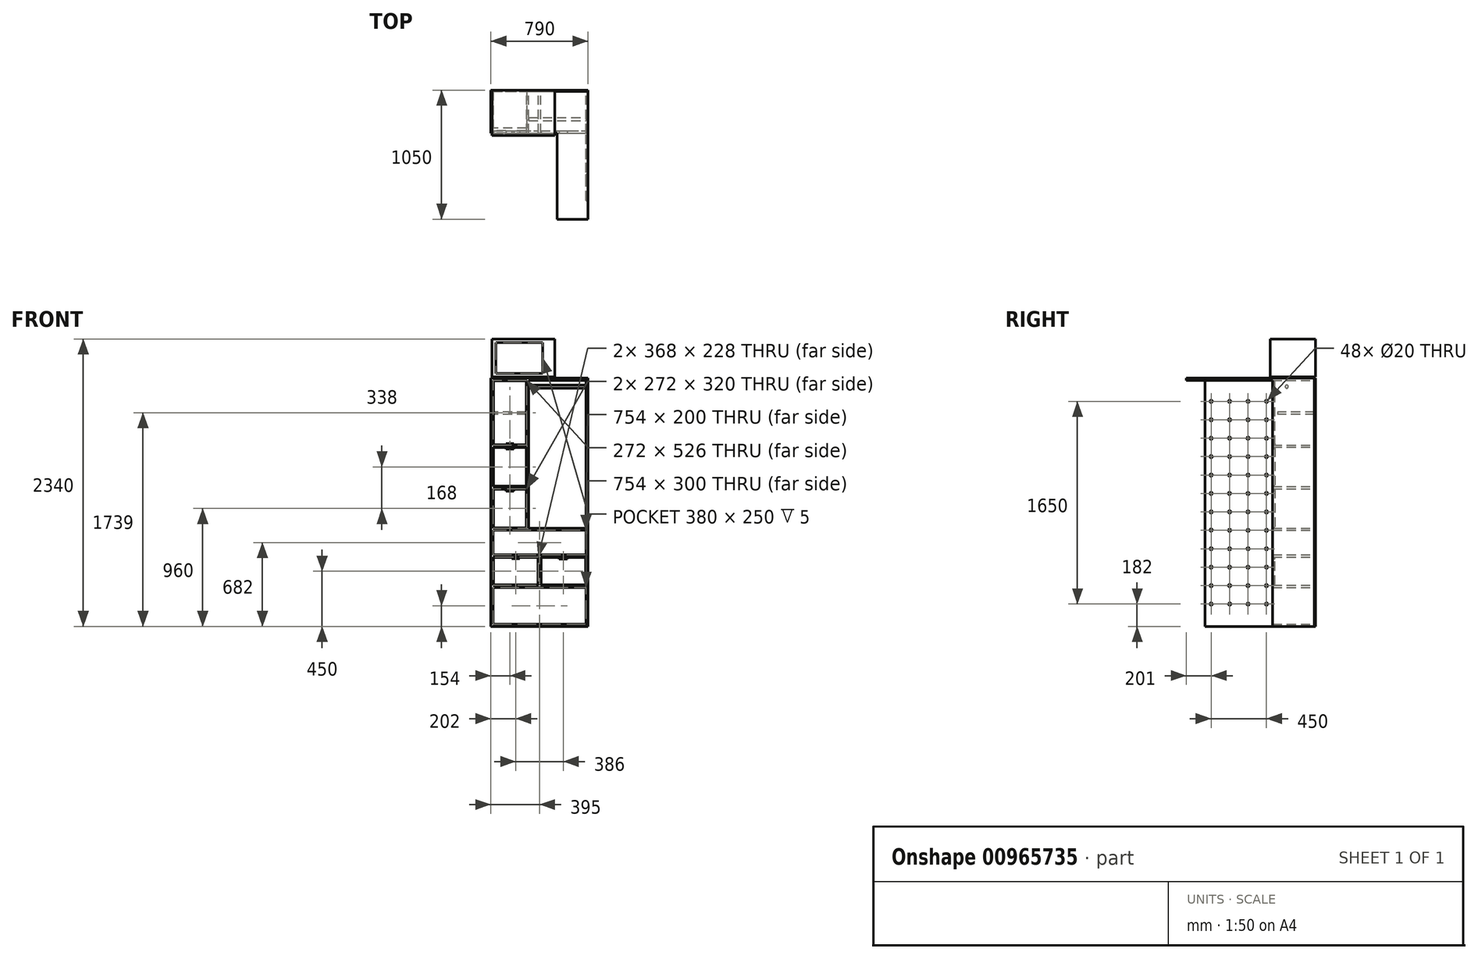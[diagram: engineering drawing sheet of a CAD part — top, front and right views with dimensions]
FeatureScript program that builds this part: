
annotation { "Feature Type Name" : "Feature", "Feature Type Description" : "" }
export const myFeature = defineFeature(function(context is Context, id is Id, definition is map)
    precondition{}
    {
        {
            var Q0;
            Q0=qCreatedBy(makeId("Front.planeOp"),FACE);
            var sketch = newSketch(context, id + "F0", { "sketchPlane" : qUnion([Q0])});
            skLineSegment(sketch, "E0.bottom", {"start": v(0, 0) * mm, "end": v(790, 0) * mm});
            skLineSegment(sketch, "E0.top", {"start": v(0, 2020) * mm, "end": v(790, 2020) * mm});
            skLineSegment(sketch, "E0.left", {"start": v(0, 0) * mm, "end": v(0, 2020) * mm});
            skLineSegment(sketch, "E0.right", {"start": v(790, 0) * mm, "end": v(790, 2020) * mm});
            skLineSegment(sketch, "E1.0", {"start": v(18, 2002) * mm, "end": v(290, 2002) * mm});
            skLineSegment(sketch, "E1.1", {"start": v(18, 18) * mm, "end": v(18, 318) * mm});
            skLineSegment(sketch, "E1.2", {"start": v(18, 18) * mm, "end": v(772, 18) * mm});
            skLineSegment(sketch, "E1.3", {"start": v(772, 18) * mm, "end": v(772, 318) * mm});
            skLineSegment(sketch, "E2.bottom", {"start": v(18, 318) * mm, "end": v(772, 318) * mm});
            skLineSegment(sketch, "E2.top", {"start": v(18, 336) * mm, "end": v(386, 336) * mm});
            skLineSegment(sketch, "E3.bottom", {"start": v(18, 564) * mm, "end": v(386, 564) * mm});
            skLineSegment(sketch, "E3.top", {"start": v(18, 582) * mm, "end": v(772, 582) * mm});
            skLineSegment(sketch, "E4.bottom", {"start": v(18, 782) * mm, "end": v(772, 782) * mm});
            skLineSegment(sketch, "E4.top", {"start": v(18, 800) * mm, "end": v(290, 800) * mm});
            skLineSegment(sketch, "E5.left", {"start": v(308, 2002) * mm, "end": v(308, 800) * mm});
            skLineSegment(sketch, "E5.right", {"start": v(290, 2002) * mm, "end": v(290, 1476) * mm});
            skLineSegment(sketch, "E6.bottom", {"start": v(18, 1120) * mm, "end": v(290, 1120) * mm});
            skLineSegment(sketch, "E6.top", {"start": v(18, 1138) * mm, "end": v(290, 1138) * mm});
            skLineSegment(sketch, "E7.bottom", {"start": v(290, 1458) * mm, "end": v(18, 1458) * mm});
            skLineSegment(sketch, "E7.top", {"start": v(290, 1476) * mm, "end": v(18, 1476) * mm});
            skLineSegment(sketch, "E8.trimOffspring", {"start": v(308, 2002) * mm, "end": v(772, 2002) * mm});
            skLineSegment(sketch, "E9.trimOffspring", {"start": v(290, 1458) * mm, "end": v(290, 1138) * mm});
            skLineSegment(sketch, "E10.trimOffspring", {"start": v(18, 1476) * mm, "end": v(18, 2002) * mm});
            skLineSegment(sketch, "E11.trimOffspring", {"start": v(18, 1138) * mm, "end": v(18, 1458) * mm});
            skLineSegment(sketch, "E12.trimOffspring", {"start": v(290, 1120) * mm, "end": v(290, 800) * mm});
            skLineSegment(sketch, "E13.trimOffspring", {"start": v(18, 800) * mm, "end": v(18, 1120) * mm});
            skLineSegment(sketch, "E14.trimOffspring", {"start": v(308, 800) * mm, "end": v(772, 800) * mm});
            skLineSegment(sketch, "E15.trimOffspring", {"start": v(772, 800) * mm, "end": v(772, 2002) * mm});
            skLineSegment(sketch, "E16.trimOffspring", {"start": v(772, 582) * mm, "end": v(772, 782) * mm});
            skLineSegment(sketch, "E17.trimOffspring", {"start": v(18, 582) * mm, "end": v(18, 782) * mm});
            skLineSegment(sketch, "E18.trimOffspring", {"start": v(18, 336) * mm, "end": v(18, 564) * mm});
            skLineSegment(sketch, "E19.trimOffspring", {"start": v(772, 336) * mm, "end": v(772, 564) * mm});
            skLineSegment(sketch, "E20.left", {"start": v(386, 564) * mm, "end": v(386, 336) * mm});
            skLineSegment(sketch, "E20.right", {"start": v(404, 564) * mm, "end": v(404, 336) * mm});
            skLineSegment(sketch, "E21.trimOffspring", {"start": v(404, 564) * mm, "end": v(772, 564) * mm});
            skLineSegment(sketch, "E22.trimOffspring", {"start": v(404, 336) * mm, "end": v(772, 336) * mm});
            skSolve(sketch);
        }
        {
            var Q0;
            Q0 = qSketchRegion(id + "F0", true);
            extrude(context, id + "F1", {"entities" : qUnion([Q0]), "depth" : 340 * mm, "offsetDistance" : 25 * mm});
        }
        {
            var Q0;
            Q0=makeQuery(id+"F1.opExtrude","CAP_FACE",FACE,{"disambiguationData":[OSD([sQuery(id+"F0.wireOp",EDGE,"E0.bottom"),sQuery(id+"F0.wireOp",EDGE,"E0.top"),sQuery(id+"F0.wireOp",EDGE,"E0.left"),sQuery(id+"F0.wireOp",EDGE,"E0.right"),sQuery(id+"F0.wireOp",EDGE,"E1.0"),sQuery(id+"F0.wireOp",EDGE,"E1.1"),sQuery(id+"F0.wireOp",EDGE,"E1.2"),sQuery(id+"F0.wireOp",EDGE,"E1.3"),sQuery(id+"F0.wireOp",EDGE,"E2.bottom"),sQuery(id+"F0.wireOp",EDGE,"E2.top"),sQuery(id+"F0.wireOp",EDGE,"E3.bottom"),sQuery(id+"F0.wireOp",EDGE,"E3.top"),sQuery(id+"F0.wireOp",EDGE,"E4.bottom"),sQuery(id+"F0.wireOp",EDGE,"E4.top"),sQuery(id+"F0.wireOp",EDGE,"E5.left"),sQuery(id+"F0.wireOp",EDGE,"E5.right"),sQuery(id+"F0.wireOp",EDGE,"E6.bottom"),sQuery(id+"F0.wireOp",EDGE,"E6.top"),sQuery(id+"F0.wireOp",EDGE,"E7.bottom"),sQuery(id+"F0.wireOp",EDGE,"E7.top"),sQuery(id+"F0.wireOp",EDGE,"E8.trimOffspring"),sQuery(id+"F0.wireOp",EDGE,"E9.trimOffspring"),sQuery(id+"F0.wireOp",EDGE,"E10.trimOffspring"),sQuery(id+"F0.wireOp",EDGE,"E11.trimOffspring"),sQuery(id+"F0.wireOp",EDGE,"E12.trimOffspring"),sQuery(id+"F0.wireOp",EDGE,"E13.trimOffspring"),sQuery(id+"F0.wireOp",EDGE,"E14.trimOffspring"),sQuery(id+"F0.wireOp",EDGE,"E15.trimOffspring"),sQuery(id+"F0.wireOp",EDGE,"E16.trimOffspring"),sQuery(id+"F0.wireOp",EDGE,"E17.trimOffspring"),sQuery(id+"F0.wireOp",EDGE,"E18.trimOffspring"),sQuery(id+"F0.wireOp",EDGE,"E19.trimOffspring"),sQuery(id+"F0.wireOp",EDGE,"E20.left"),sQuery(id+"F0.wireOp",EDGE,"E20.right"),sQuery(id+"F0.wireOp",EDGE,"E21.trimOffspring"),sQuery(id+"F0.wireOp",EDGE,"E22.trimOffspring")])],"isStart":true});
            var sketch = newSketch(context, id + "F2", { "sketchPlane" : qUnion([Q0])});
            skLineSegment(sketch, "E23.bottom", {"start": v(-790, 2020) * mm, "end": v(0, 2020) * mm});
            skLineSegment(sketch, "E23.top", {"start": v(-790, 0) * mm, "end": v(0, 0) * mm});
            skLineSegment(sketch, "E23.left", {"start": v(-790, 2020) * mm, "end": v(-790, 0) * mm});
            skLineSegment(sketch, "E23.right", {"start": v(0, 2020) * mm, "end": v(0, 0) * mm});
            skSolve(sketch);
        }
        {
            var Q0;
            Q0 = qSketchRegion(id + "F2", true);
            extrude(context, id + "F3", {"entities" : qUnion([Q0]), "depth" : 9 * mm, "offsetDistance" : 25 * mm});
        }
        {
            var Q0;
            Q0=makeQuery(id+"F1.opExtrude","SWEPT_FACE",FACE,{"disambiguationData":[OSD([sQuery(id+"F0.wireOp",EDGE,"E0.top")])]});
            var sketch = newSketch(context, id + "F4", { "sketchPlane" : qUnion([Q0])});
            skLineSegment(sketch, "E24.bottom", {"start": v(790, -340) * mm, "end": v(540, -340) * mm});
            skLineSegment(sketch, "E24.top", {"start": v(790, -1041) * mm, "end": v(540, -1041) * mm});
            skLineSegment(sketch, "E24.left", {"start": v(790, -340) * mm, "end": v(790, -1041) * mm});
            skLineSegment(sketch, "E24.right", {"start": v(540, -340) * mm, "end": v(540, -1041) * mm});
            skSolve(sketch);
        }
        {
            var Q0;
            Q0 = qSketchRegion(id + "F4", true);
            extrude(context, id + "F5", {"entities" : qUnion([Q0]), "operationType" : NewBodyOperationType.ADD, "oppositeDirection" : true, "depth" : 18 * mm, "offsetDistance" : 25 * mm});
        }
        {
            var Q0;
            Q0=makeQuery(id+"F5.boolean.opBoolean","MERGE",FACE,{"derivedFrom":[makeQuery(id+"F1.opExtrude","SWEPT_FACE",FACE,{"disambiguationData":[OSD([sQuery(id+"F0.wireOp",EDGE,"E8.trimOffspring")])]}),makeQuery(id+"F5.opExtrude","CAP_FACE",FACE,{"disambiguationData":[OSD([sQuery(id+"F4.wireOp",EDGE,"E24.bottom"),sQuery(id+"F4.wireOp",EDGE,"E24.top"),sQuery(id+"F4.wireOp",EDGE,"E24.left"),sQuery(id+"F4.wireOp",EDGE,"E24.right")])],"isStart":false})]});
            var sketch = newSketch(context, id + "F6", { "sketchPlane" : qUnion([Q0])});
            skLineSegment(sketch, "E25.bottom", {"start": v(772, 340) * mm, "end": v(790, 340) * mm});
            skLineSegment(sketch, "E25.top", {"start": v(772, 890) * mm, "end": v(790, 890) * mm});
            skLineSegment(sketch, "E25.left", {"start": v(772, 340) * mm, "end": v(772, 890) * mm});
            skLineSegment(sketch, "E25.right", {"start": v(790, 340) * mm, "end": v(790, 890) * mm});
            skSolve(sketch);
        }
        {
            var Q0;
            Q0 = qSketchRegion(id + "F6", true);
            extrude(context, id + "F7", {"entities" : qUnion([Q0]), "depth" : 2002 * mm, "offsetDistance" : 25 * mm});
        }
        {
            var Q0;
            Q0=makeQuery(id+"F7.opExtrude","SWEPT_FACE",FACE,{"disambiguationData":[OSD([sQuery(id+"F6.wireOp",EDGE,"E25.left")])]});
            var sketch = newSketch(context, id + "F8", { "sketchPlane" : qUnion([Q0])});
            skLineSegment(sketch, "E26.bottom", {"start": v(890, 0) * mm, "end": v(340, 0) * mm, "construction": true});
            skLineSegment(sketch, "E26.top", {"start": v(890, 2002) * mm, "end": v(340, 2002) * mm, "construction": true});
            skLineSegment(sketch, "E26.left", {"start": v(890, 0) * mm, "end": v(890, 2002) * mm, "construction": true});
            skLineSegment(sketch, "E26.right", {"start": v(340, 0) * mm, "end": v(340, 2002) * mm, "construction": true});
            skLineSegment(sketch, "E27", {"start": v(390, 2002) * mm, "end": v(390, 0) * mm, "construction": true});
            skLineSegment(sketch, "E28", {"start": v(540, 2002) * mm, "end": v(540, 0) * mm, "construction": true});
            skLineSegment(sketch, "E29", {"start": v(690, 2002) * mm, "end": v(690, 0) * mm, "construction": true});
            skLineSegment(sketch, "E30", {"start": v(840, 2002) * mm, "end": v(840, 0) * mm, "construction": true});
            skLineSegment(sketch, "E31", {"start": v(340, 1832) * mm, "end": v(890, 1832) * mm, "construction": true});
            skLineSegment(sketch, "E32", {"start": v(340, 1682) * mm, "end": v(890, 1682) * mm, "construction": true});
            skLineSegment(sketch, "E33", {"start": v(340, 1532) * mm, "end": v(890, 1532) * mm, "construction": true});
            skLineSegment(sketch, "E34", {"start": v(340, 1382) * mm, "end": v(890, 1382) * mm, "construction": true});
            skLineSegment(sketch, "E35", {"start": v(340, 1232) * mm, "end": v(890, 1232) * mm, "construction": true});
            skLineSegment(sketch, "E36", {"start": v(340, 1082) * mm, "end": v(890, 1082) * mm, "construction": true});
            skLineSegment(sketch, "E37", {"start": v(340, 932) * mm, "end": v(890, 932) * mm, "construction": true});
            skLineSegment(sketch, "E38", {"start": v(340, 782) * mm, "end": v(890, 782) * mm, "construction": true});
            skLineSegment(sketch, "E39", {"start": v(340, 632) * mm, "end": v(890, 632) * mm, "construction": true});
            skLineSegment(sketch, "E40", {"start": v(340, 482) * mm, "end": v(890, 482) * mm, "construction": true});
            skLineSegment(sketch, "E41", {"start": v(340, 332) * mm, "end": v(890, 332) * mm, "construction": true});
            skLineSegment(sketch, "E42", {"start": v(340, 182) * mm, "end": v(890, 182) * mm, "construction": true});
            skCircle(sketch, "E43", {"center": v(390, 1832) * mm, "radius": 10 * mm});
            skCircle(sketch, "E44", {"center": v(540, 1832) * mm, "radius": 10 * mm});
            skCircle(sketch, "E45", {"center": v(690, 1832) * mm, "radius": 10 * mm});
            skCircle(sketch, "E46", {"center": v(840, 1832) * mm, "radius": 10 * mm});
            skCircle(sketch, "E47", {"center": v(840, 1682) * mm, "radius": 10 * mm});
            skCircle(sketch, "E48", {"center": v(840, 1532) * mm, "radius": 10 * mm});
            skCircle(sketch, "E49", {"center": v(840, 1382) * mm, "radius": 10 * mm});
            skCircle(sketch, "E50", {"center": v(840, 1232) * mm, "radius": 10 * mm});
            skCircle(sketch, "E51", {"center": v(840, 1082) * mm, "radius": 10 * mm});
            skCircle(sketch, "E52", {"center": v(840, 932) * mm, "radius": 10 * mm});
            skCircle(sketch, "E53", {"center": v(840, 784.34) * mm, "radius": 10 * mm});
            skCircle(sketch, "E54", {"center": v(840, 632) * mm, "radius": 10 * mm});
            skCircle(sketch, "E55", {"center": v(840, 482) * mm, "radius": 10 * mm});
            skCircle(sketch, "E56", {"center": v(840, 332) * mm, "radius": 10 * mm});
            skCircle(sketch, "E57", {"center": v(840, 182) * mm, "radius": 10 * mm});
            skCircle(sketch, "E58", {"center": v(688.75, 182) * mm, "radius": 10 * mm});
            skCircle(sketch, "E59", {"center": v(540, 182) * mm, "radius": 10 * mm});
            skCircle(sketch, "E60", {"center": v(390, 182) * mm, "radius": 10 * mm});
            skCircle(sketch, "E61", {"center": v(390, 332) * mm, "radius": 10 * mm});
            skCircle(sketch, "E62", {"center": v(540, 332) * mm, "radius": 10 * mm});
            skCircle(sketch, "E63", {"center": v(690, 332) * mm, "radius": 10 * mm});
            skCircle(sketch, "E64", {"center": v(690, 482) * mm, "radius": 10 * mm});
            skCircle(sketch, "E65", {"center": v(540, 482) * mm, "radius": 10 * mm});
            skCircle(sketch, "E66", {"center": v(390, 482) * mm, "radius": 10 * mm});
            skCircle(sketch, "E67", {"center": v(390, 632) * mm, "radius": 10 * mm});
            skCircle(sketch, "E68", {"center": v(540, 632) * mm, "radius": 10 * mm});
            skCircle(sketch, "E69", {"center": v(690, 632) * mm, "radius": 10 * mm});
            skCircle(sketch, "E70", {"center": v(690, 782) * mm, "radius": 10 * mm});
            skCircle(sketch, "E71", {"center": v(540, 782) * mm, "radius": 10 * mm});
            skCircle(sketch, "E72", {"center": v(390, 782) * mm, "radius": 10 * mm});
            skCircle(sketch, "E73", {"center": v(390, 932) * mm, "radius": 10 * mm});
            skCircle(sketch, "E74", {"center": v(540, 932) * mm, "radius": 10 * mm});
            skCircle(sketch, "E75", {"center": v(690, 932) * mm, "radius": 10 * mm});
            skCircle(sketch, "E76", {"center": v(691.04, 1082) * mm, "radius": 10 * mm});
            skCircle(sketch, "E77", {"center": v(540, 1082) * mm, "radius": 10 * mm});
            skCircle(sketch, "E78", {"center": v(390, 1082) * mm, "radius": 10 * mm});
            skCircle(sketch, "E79", {"center": v(390, 1232) * mm, "radius": 10 * mm});
            skCircle(sketch, "E80", {"center": v(390, 1382) * mm, "radius": 10 * mm});
            skCircle(sketch, "E81", {"center": v(390, 1532) * mm, "radius": 10 * mm});
            skCircle(sketch, "E82", {"center": v(390, 1682) * mm, "radius": 10 * mm});
            skCircle(sketch, "E83", {"center": v(540, 1682) * mm, "radius": 10 * mm});
            skCircle(sketch, "E84", {"center": v(540, 1532) * mm, "radius": 10 * mm});
            skCircle(sketch, "E85", {"center": v(540, 1382) * mm, "radius": 10 * mm});
            skCircle(sketch, "E86", {"center": v(540, 1232) * mm, "radius": 10 * mm});
            skCircle(sketch, "E87", {"center": v(690, 1232) * mm, "radius": 10 * mm});
            skCircle(sketch, "E88", {"center": v(690, 1382) * mm, "radius": 10 * mm});
            skCircle(sketch, "E89", {"center": v(690, 1532) * mm, "radius": 10 * mm});
            skCircle(sketch, "E90", {"center": v(690, 1682) * mm, "radius": 10 * mm});
            skSolve(sketch);
        }
        {
            var Q0;
            Q0 = qSketchRegion(id + "F8", true);
            extrude(context, id + "F9", {"entities" : qUnion([Q0]), "operationType" : NewBodyOperationType.REMOVE, "oppositeDirection" : true, "depth" : 18 * mm, "offsetDistance" : 25 * mm});
        }
        {
            var Q0;
            Q0=makeQuery(id+"F9.boolean.opBoolean","COPY",EDGE,{"derivedFrom":makeQuery(id+"F9.opExtrude","CAP_EDGE",EDGE,{"disambiguationData":[OSD([sQuery(id+"F8.wireOp",EDGE,"E43")])],"isStart":true})});
            var Q1;
            Q1=makeQuery(id+"F9.boolean.opBoolean","COPY",EDGE,{"derivedFrom":makeQuery(id+"F9.opExtrude","CAP_EDGE",EDGE,{"disambiguationData":[OSD([sQuery(id+"F8.wireOp",EDGE,"E44")])],"isStart":true})});
            var Q2;
            Q2=makeQuery(id+"F9.boolean.opBoolean","COPY",EDGE,{"derivedFrom":makeQuery(id+"F9.opExtrude","CAP_EDGE",EDGE,{"disambiguationData":[OSD([sQuery(id+"F8.wireOp",EDGE,"E45")])],"isStart":true})});
            var Q3;
            Q3=makeQuery(id+"F9.boolean.opBoolean","COPY",EDGE,{"derivedFrom":makeQuery(id+"F9.opExtrude","CAP_EDGE",EDGE,{"disambiguationData":[OSD([sQuery(id+"F8.wireOp",EDGE,"E46")])],"isStart":true})});
            var Q4;
            Q4=makeQuery(id+"F9.boolean.opBoolean","COPY",EDGE,{"derivedFrom":makeQuery(id+"F9.opExtrude","CAP_EDGE",EDGE,{"disambiguationData":[OSD([sQuery(id+"F8.wireOp",EDGE,"E47")])],"isStart":true})});
            var Q5;
            Q5=makeQuery(id+"F9.boolean.opBoolean","COPY",EDGE,{"derivedFrom":makeQuery(id+"F9.opExtrude","CAP_EDGE",EDGE,{"disambiguationData":[OSD([sQuery(id+"F8.wireOp",EDGE,"E90")])],"isStart":true})});
            var Q6;
            Q6=makeQuery(id+"F9.boolean.opBoolean","COPY",EDGE,{"derivedFrom":makeQuery(id+"F9.opExtrude","CAP_EDGE",EDGE,{"disambiguationData":[OSD([sQuery(id+"F8.wireOp",EDGE,"E83")])],"isStart":true})});
            var Q7;
            Q7=makeQuery(id+"F9.boolean.opBoolean","COPY",EDGE,{"derivedFrom":makeQuery(id+"F9.opExtrude","CAP_EDGE",EDGE,{"disambiguationData":[OSD([sQuery(id+"F8.wireOp",EDGE,"E82")])],"isStart":true})});
            var Q8;
            Q8=makeQuery(id+"F9.boolean.opBoolean","COPY",EDGE,{"derivedFrom":makeQuery(id+"F9.opExtrude","CAP_EDGE",EDGE,{"disambiguationData":[OSD([sQuery(id+"F8.wireOp",EDGE,"E81")])],"isStart":true})});
            var Q9;
            Q9=makeQuery(id+"F9.boolean.opBoolean","COPY",EDGE,{"derivedFrom":makeQuery(id+"F9.opExtrude","CAP_EDGE",EDGE,{"disambiguationData":[OSD([sQuery(id+"F8.wireOp",EDGE,"E84")])],"isStart":true})});
            var Q10;
            Q10=makeQuery(id+"F9.boolean.opBoolean","COPY",EDGE,{"derivedFrom":makeQuery(id+"F9.opExtrude","CAP_EDGE",EDGE,{"disambiguationData":[OSD([sQuery(id+"F8.wireOp",EDGE,"E89")])],"isStart":true})});
            var Q11;
            Q11=makeQuery(id+"F9.boolean.opBoolean","COPY",EDGE,{"derivedFrom":makeQuery(id+"F9.opExtrude","CAP_EDGE",EDGE,{"disambiguationData":[OSD([sQuery(id+"F8.wireOp",EDGE,"E48")])],"isStart":true})});
            var Q12;
            Q12=makeQuery(id+"F9.boolean.opBoolean","COPY",EDGE,{"derivedFrom":makeQuery(id+"F9.opExtrude","CAP_EDGE",EDGE,{"disambiguationData":[OSD([sQuery(id+"F8.wireOp",EDGE,"E49")])],"isStart":true})});
            var Q13;
            Q13=makeQuery(id+"F9.boolean.opBoolean","COPY",EDGE,{"derivedFrom":makeQuery(id+"F9.opExtrude","CAP_EDGE",EDGE,{"disambiguationData":[OSD([sQuery(id+"F8.wireOp",EDGE,"E88")])],"isStart":true})});
            var Q14;
            Q14=makeQuery(id+"F9.boolean.opBoolean","COPY",EDGE,{"derivedFrom":makeQuery(id+"F9.opExtrude","CAP_EDGE",EDGE,{"disambiguationData":[OSD([sQuery(id+"F8.wireOp",EDGE,"E85")])],"isStart":true})});
            var Q15;
            Q15=makeQuery(id+"F9.boolean.opBoolean","COPY",EDGE,{"derivedFrom":makeQuery(id+"F9.opExtrude","CAP_EDGE",EDGE,{"disambiguationData":[OSD([sQuery(id+"F8.wireOp",EDGE,"E80")])],"isStart":true})});
            var Q16;
            Q16=makeQuery(id+"F9.boolean.opBoolean","COPY",EDGE,{"derivedFrom":makeQuery(id+"F9.opExtrude","CAP_EDGE",EDGE,{"disambiguationData":[OSD([sQuery(id+"F8.wireOp",EDGE,"E79")])],"isStart":true})});
            var Q17;
            Q17=makeQuery(id+"F9.boolean.opBoolean","COPY",EDGE,{"derivedFrom":makeQuery(id+"F9.opExtrude","CAP_EDGE",EDGE,{"disambiguationData":[OSD([sQuery(id+"F8.wireOp",EDGE,"E86")])],"isStart":true})});
            var Q18;
            Q18=makeQuery(id+"F9.boolean.opBoolean","COPY",EDGE,{"derivedFrom":makeQuery(id+"F9.opExtrude","CAP_EDGE",EDGE,{"disambiguationData":[OSD([sQuery(id+"F8.wireOp",EDGE,"E87")])],"isStart":true})});
            var Q19;
            Q19=makeQuery(id+"F9.boolean.opBoolean","COPY",EDGE,{"derivedFrom":makeQuery(id+"F9.opExtrude","CAP_EDGE",EDGE,{"disambiguationData":[OSD([sQuery(id+"F8.wireOp",EDGE,"E50")])],"isStart":true})});
            var Q20;
            Q20=makeQuery(id+"F9.boolean.opBoolean","COPY",EDGE,{"derivedFrom":makeQuery(id+"F9.opExtrude","CAP_EDGE",EDGE,{"disambiguationData":[OSD([sQuery(id+"F8.wireOp",EDGE,"E51")])],"isStart":true})});
            var Q21;
            Q21=makeQuery(id+"F9.boolean.opBoolean","COPY",EDGE,{"derivedFrom":makeQuery(id+"F9.opExtrude","CAP_EDGE",EDGE,{"disambiguationData":[OSD([sQuery(id+"F8.wireOp",EDGE,"E76")])],"isStart":true})});
            var Q22;
            Q22=makeQuery(id+"F9.boolean.opBoolean","COPY",EDGE,{"derivedFrom":makeQuery(id+"F9.opExtrude","CAP_EDGE",EDGE,{"disambiguationData":[OSD([sQuery(id+"F8.wireOp",EDGE,"E77")])],"isStart":true})});
            var Q23;
            Q23=makeQuery(id+"F9.boolean.opBoolean","COPY",EDGE,{"derivedFrom":makeQuery(id+"F9.opExtrude","CAP_EDGE",EDGE,{"disambiguationData":[OSD([sQuery(id+"F8.wireOp",EDGE,"E78")])],"isStart":true})});
            var Q24;
            Q24=makeQuery(id+"F9.boolean.opBoolean","COPY",EDGE,{"derivedFrom":makeQuery(id+"F9.opExtrude","CAP_EDGE",EDGE,{"disambiguationData":[OSD([sQuery(id+"F8.wireOp",EDGE,"E73")])],"isStart":true})});
            var Q25;
            Q25=makeQuery(id+"F9.boolean.opBoolean","COPY",EDGE,{"derivedFrom":makeQuery(id+"F9.opExtrude","CAP_EDGE",EDGE,{"disambiguationData":[OSD([sQuery(id+"F8.wireOp",EDGE,"E74")])],"isStart":false})});
            var Q26;
            Q26=makeQuery(id+"F9.boolean.opBoolean","COPY",EDGE,{"derivedFrom":makeQuery(id+"F9.opExtrude","CAP_EDGE",EDGE,{"disambiguationData":[OSD([sQuery(id+"F8.wireOp",EDGE,"E74")])],"isStart":true})});
            var Q27;
            Q27=makeQuery(id+"F9.boolean.opBoolean","COPY",EDGE,{"derivedFrom":makeQuery(id+"F9.opExtrude","CAP_EDGE",EDGE,{"disambiguationData":[OSD([sQuery(id+"F8.wireOp",EDGE,"E52")])],"isStart":true})});
            var Q28;
            Q28=makeQuery(id+"F7.opExtrude","SWEPT_FACE",FACE,{"disambiguationData":[OSD([sQuery(id+"F6.wireOp",EDGE,"E25.left")])]});
            var Q29;
            Q29=makeQuery(id+"F9.boolean.opBoolean","COPY",EDGE,{"derivedFrom":makeQuery(id+"F9.opExtrude","CAP_EDGE",EDGE,{"disambiguationData":[OSD([sQuery(id+"F8.wireOp",EDGE,"E70")])],"isStart":true})});
            var Q30;
            Q30=makeQuery(id+"F9.boolean.opBoolean","COPY",EDGE,{"derivedFrom":makeQuery(id+"F9.opExtrude","CAP_EDGE",EDGE,{"disambiguationData":[OSD([sQuery(id+"F8.wireOp",EDGE,"E75")])],"isStart":true})});
            var Q31;
            Q31=makeQuery(id+"F9.boolean.opBoolean","COPY",EDGE,{"derivedFrom":makeQuery(id+"F9.opExtrude","CAP_EDGE",EDGE,{"disambiguationData":[OSD([sQuery(id+"F8.wireOp",EDGE,"E53")])],"isStart":true})});
            var Q32;
            Q32=makeQuery(id+"F9.boolean.opBoolean","COPY",EDGE,{"derivedFrom":makeQuery(id+"F9.opExtrude","CAP_EDGE",EDGE,{"disambiguationData":[OSD([sQuery(id+"F8.wireOp",EDGE,"E71")])],"isStart":true})});
            var Q33;
            Q33=makeQuery(id+"F9.boolean.opBoolean","COPY",EDGE,{"derivedFrom":makeQuery(id+"F9.opExtrude","CAP_EDGE",EDGE,{"disambiguationData":[OSD([sQuery(id+"F8.wireOp",EDGE,"E72")])],"isStart":true})});
            var Q34;
            Q34=makeQuery(id+"F9.boolean.opBoolean","COPY",EDGE,{"derivedFrom":makeQuery(id+"F9.opExtrude","CAP_EDGE",EDGE,{"disambiguationData":[OSD([sQuery(id+"F8.wireOp",EDGE,"E57")])],"isStart":true})});
            var Q35;
            Q35=makeQuery(id+"F9.boolean.opBoolean","COPY",EDGE,{"derivedFrom":makeQuery(id+"F9.opExtrude","CAP_EDGE",EDGE,{"disambiguationData":[OSD([sQuery(id+"F8.wireOp",EDGE,"E58")])],"isStart":true})});
            var Q36;
            Q36=makeQuery(id+"F9.boolean.opBoolean","COPY",EDGE,{"derivedFrom":makeQuery(id+"F9.opExtrude","CAP_EDGE",EDGE,{"disambiguationData":[OSD([sQuery(id+"F8.wireOp",EDGE,"E59")])],"isStart":true})});
            var Q37;
            Q37=makeQuery(id+"F9.boolean.opBoolean","COPY",EDGE,{"derivedFrom":makeQuery(id+"F9.opExtrude","CAP_EDGE",EDGE,{"disambiguationData":[OSD([sQuery(id+"F8.wireOp",EDGE,"E60")])],"isStart":true})});
            var Q38;
            Q38=makeQuery(id+"F9.boolean.opBoolean","COPY",EDGE,{"derivedFrom":makeQuery(id+"F9.opExtrude","CAP_EDGE",EDGE,{"disambiguationData":[OSD([sQuery(id+"F8.wireOp",EDGE,"E61")])],"isStart":true})});
            var Q39;
            Q39=makeQuery(id+"F9.boolean.opBoolean","COPY",EDGE,{"derivedFrom":makeQuery(id+"F9.opExtrude","CAP_EDGE",EDGE,{"disambiguationData":[OSD([sQuery(id+"F8.wireOp",EDGE,"E62")])],"isStart":true})});
            var Q40;
            Q40=makeQuery(id+"F9.boolean.opBoolean","COPY",EDGE,{"derivedFrom":makeQuery(id+"F9.opExtrude","CAP_EDGE",EDGE,{"disambiguationData":[OSD([sQuery(id+"F8.wireOp",EDGE,"E63")])],"isStart":true})});
            var Q41;
            Q41=makeQuery(id+"F9.boolean.opBoolean","COPY",EDGE,{"derivedFrom":makeQuery(id+"F9.opExtrude","CAP_EDGE",EDGE,{"disambiguationData":[OSD([sQuery(id+"F8.wireOp",EDGE,"E56")])],"isStart":true})});
            var Q42;
            Q42=makeQuery(id+"F9.boolean.opBoolean","COPY",EDGE,{"derivedFrom":makeQuery(id+"F9.opExtrude","CAP_EDGE",EDGE,{"disambiguationData":[OSD([sQuery(id+"F8.wireOp",EDGE,"E55")])],"isStart":true})});
            var Q43;
            Q43=makeQuery(id+"F9.boolean.opBoolean","COPY",EDGE,{"derivedFrom":makeQuery(id+"F9.opExtrude","CAP_EDGE",EDGE,{"disambiguationData":[OSD([sQuery(id+"F8.wireOp",EDGE,"E64")])],"isStart":true})});
            var Q44;
            Q44=makeQuery(id+"F9.boolean.opBoolean","COPY",EDGE,{"derivedFrom":makeQuery(id+"F9.opExtrude","CAP_EDGE",EDGE,{"disambiguationData":[OSD([sQuery(id+"F8.wireOp",EDGE,"E65")])],"isStart":true})});
            var Q45;
            Q45=makeQuery(id+"F9.boolean.opBoolean","COPY",EDGE,{"derivedFrom":makeQuery(id+"F9.opExtrude","CAP_EDGE",EDGE,{"disambiguationData":[OSD([sQuery(id+"F8.wireOp",EDGE,"E66")])],"isStart":true})});
            var Q46;
            Q46=makeQuery(id+"F9.boolean.opBoolean","COPY",EDGE,{"derivedFrom":makeQuery(id+"F9.opExtrude","CAP_EDGE",EDGE,{"disambiguationData":[OSD([sQuery(id+"F8.wireOp",EDGE,"E67")])],"isStart":true})});
            var Q47;
            Q47=makeQuery(id+"F9.boolean.opBoolean","COPY",EDGE,{"derivedFrom":makeQuery(id+"F9.opExtrude","CAP_EDGE",EDGE,{"disambiguationData":[OSD([sQuery(id+"F8.wireOp",EDGE,"E68")])],"isStart":true})});
            var Q48;
            Q48=makeQuery(id+"F9.boolean.opBoolean","COPY",EDGE,{"derivedFrom":makeQuery(id+"F9.opExtrude","CAP_EDGE",EDGE,{"disambiguationData":[OSD([sQuery(id+"F8.wireOp",EDGE,"E69")])],"isStart":true})});
            var Q49;
            Q49=makeQuery(id+"F9.boolean.opBoolean","COPY",EDGE,{"derivedFrom":makeQuery(id+"F9.opExtrude","CAP_EDGE",EDGE,{"disambiguationData":[OSD([sQuery(id+"F8.wireOp",EDGE,"E54")])],"isStart":true})});
            chamfer(context, id + "F10", {"entities" : qUnion([Q0, Q1, Q2, Q3, Q4, Q5, Q6, Q7, Q8, Q9, Q10, Q11, Q12, Q13, Q14, Q15, Q16, Q17, Q18, Q19, Q20, Q21, Q22, Q23, Q24, Q25, Q26, Q27, Q28, Q29, Q30, Q31, Q32, Q33, Q34, Q35, Q36, Q37, Q38, Q39, Q40, Q41, Q42, Q43, Q44, Q45, Q46, Q47, Q48, Q49]), "width" : 3 * mm, "tangentPropagation" : true});
        }
        {
            var Q0;
            Q0=makeQuery(id+"F1.opExtrude","CAP_FACE",FACE,{"disambiguationData":[OSD([sQuery(id+"F0.wireOp",EDGE,"E0.bottom"),sQuery(id+"F0.wireOp",EDGE,"E0.top"),sQuery(id+"F0.wireOp",EDGE,"E0.left"),sQuery(id+"F0.wireOp",EDGE,"E0.right"),sQuery(id+"F0.wireOp",EDGE,"E1.0"),sQuery(id+"F0.wireOp",EDGE,"E1.1"),sQuery(id+"F0.wireOp",EDGE,"E1.2"),sQuery(id+"F0.wireOp",EDGE,"E1.3"),sQuery(id+"F0.wireOp",EDGE,"E2.bottom"),sQuery(id+"F0.wireOp",EDGE,"E2.top"),sQuery(id+"F0.wireOp",EDGE,"E3.bottom"),sQuery(id+"F0.wireOp",EDGE,"E3.top"),sQuery(id+"F0.wireOp",EDGE,"E4.bottom"),sQuery(id+"F0.wireOp",EDGE,"E4.top"),sQuery(id+"F0.wireOp",EDGE,"E5.left"),sQuery(id+"F0.wireOp",EDGE,"E5.right"),sQuery(id+"F0.wireOp",EDGE,"E6.bottom"),sQuery(id+"F0.wireOp",EDGE,"E6.top"),sQuery(id+"F0.wireOp",EDGE,"E7.bottom"),sQuery(id+"F0.wireOp",EDGE,"E7.top"),sQuery(id+"F0.wireOp",EDGE,"E8.trimOffspring"),sQuery(id+"F0.wireOp",EDGE,"E9.trimOffspring"),sQuery(id+"F0.wireOp",EDGE,"E10.trimOffspring"),sQuery(id+"F0.wireOp",EDGE,"E11.trimOffspring"),sQuery(id+"F0.wireOp",EDGE,"E12.trimOffspring"),sQuery(id+"F0.wireOp",EDGE,"E13.trimOffspring"),sQuery(id+"F0.wireOp",EDGE,"E14.trimOffspring"),sQuery(id+"F0.wireOp",EDGE,"E15.trimOffspring"),sQuery(id+"F0.wireOp",EDGE,"E16.trimOffspring"),sQuery(id+"F0.wireOp",EDGE,"E17.trimOffspring"),sQuery(id+"F0.wireOp",EDGE,"E18.trimOffspring"),sQuery(id+"F0.wireOp",EDGE,"E19.trimOffspring"),sQuery(id+"F0.wireOp",EDGE,"E20.left"),sQuery(id+"F0.wireOp",EDGE,"E20.right"),sQuery(id+"F0.wireOp",EDGE,"E21.trimOffspring"),sQuery(id+"F0.wireOp",EDGE,"E22.trimOffspring")])],"isStart":false});
            var sketch = newSketch(context, id + "F11", { "sketchPlane" : qUnion([Q0])});
            skLineSegment(sketch, "E91.0", {"start": v(21, 1479) * mm, "end": v(21, 1999) * mm});
            skLineSegment(sketch, "E91.1", {"start": v(287, 1479) * mm, "end": v(21, 1479) * mm});
            skLineSegment(sketch, "E91.2", {"start": v(287, 1999) * mm, "end": v(287, 1479) * mm});
            skLineSegment(sketch, "E91.3", {"start": v(21, 1999) * mm, "end": v(287, 1999) * mm});
            skLineSegment(sketch, "E92.0", {"start": v(21, 1141) * mm, "end": v(21, 1455) * mm});
            skLineSegment(sketch, "E92.1", {"start": v(21, 1141) * mm, "end": v(287, 1141) * mm});
            skLineSegment(sketch, "E92.2", {"start": v(287, 1455) * mm, "end": v(287, 1141) * mm});
            skLineSegment(sketch, "E92.3", {"start": v(287, 1455) * mm, "end": v(21, 1455) * mm});
            skLineSegment(sketch, "E93.0", {"start": v(21, 1117) * mm, "end": v(287, 1117) * mm});
            skLineSegment(sketch, "E93.1", {"start": v(21, 803) * mm, "end": v(21, 1117) * mm});
            skLineSegment(sketch, "E93.2", {"start": v(21, 803) * mm, "end": v(287, 803) * mm});
            skLineSegment(sketch, "E93.3", {"start": v(287, 1117) * mm, "end": v(287, 803) * mm});
            skLineSegment(sketch, "E94.0", {"start": v(21, 561) * mm, "end": v(383, 561) * mm});
            skLineSegment(sketch, "E94.1", {"start": v(21, 339) * mm, "end": v(21, 561) * mm});
            skLineSegment(sketch, "E94.2", {"start": v(21, 339) * mm, "end": v(383, 339) * mm});
            skLineSegment(sketch, "E94.3", {"start": v(383, 561) * mm, "end": v(383, 339) * mm});
            skLineSegment(sketch, "E95.0", {"start": v(407, 561) * mm, "end": v(769, 561) * mm});
            skLineSegment(sketch, "E95.1", {"start": v(407, 561) * mm, "end": v(407, 339) * mm});
            skLineSegment(sketch, "E95.2", {"start": v(407, 339) * mm, "end": v(769, 339) * mm});
            skLineSegment(sketch, "E95.3", {"start": v(769, 339) * mm, "end": v(769, 561) * mm});
            skSolve(sketch);
        }
        {
            var Q0;
            Q0 = qSketchRegion(id + "F11", true);
            extrude(context, id + "F12", {"entities" : qUnion([Q0]), "oppositeDirection" : true, "depth" : 18 * mm, "offsetDistance" : 25 * mm});
        }
        {
            var Q0;
            Q0=makeQuery(id+"F12.opExtrude","CAP_FACE",FACE,{"disambiguationData":[OSD([sQuery(id+"F11.wireOp",EDGE,"E94.0"),sQuery(id+"F11.wireOp",EDGE,"E94.1"),sQuery(id+"F11.wireOp",EDGE,"E94.2"),sQuery(id+"F11.wireOp",EDGE,"E94.3")])],"isStart":true});
            var sketch = newSketch(context, id + "F13", { "sketchPlane" : qUnion([Q0])});
            skPoint(sketch, "E96.centerSnap0", {"position": v(21, 450) * mm});
            skPoint(sketch, "E96.centerSnap1", {"position": v(202, 561) * mm});
            skLineSegment(sketch, "E97.bottom", {"start": v(169.5, 552.25) * mm, "end": v(234.5, 552.25) * mm});
            skPoint(sketch, "E97.left.end.orphan", {"position": v(169.5, 569.75) * mm});
            skPoint(sketch, "E97.right.end.orphan", {"position": v(234.5, 569.75) * mm});
            skLineSegment(sketch, "E98", {"start": v(234.5, 552.25) * mm, "end": v(234.5, 561) * mm});
            skLineSegment(sketch, "E99", {"start": v(234.5, 561) * mm, "end": v(169.5, 561) * mm});
            skLineSegment(sketch, "E100", {"start": v(169.5, 561) * mm, "end": v(169.5, 552.25) * mm});
            skSolve(sketch);
        }
        {
            var Q0;
            Q0 = qSketchRegion(id + "F13", true);
            extrude(context, id + "F14", {"entities" : qUnion([Q0]), "operationType" : NewBodyOperationType.REMOVE, "oppositeDirection" : true, "depth" : 25 * mm, "offsetDistance" : 25 * mm});
        }
        {
            var Q0;
            Q0=makeQuery(id+"F12.opExtrude","CAP_FACE",FACE,{"disambiguationData":[OSD([sQuery(id+"F11.wireOp",EDGE,"E95.0"),sQuery(id+"F11.wireOp",EDGE,"E95.1"),sQuery(id+"F11.wireOp",EDGE,"E95.2"),sQuery(id+"F11.wireOp",EDGE,"E95.3")])],"isStart":true});
            var sketch = newSketch(context, id + "F15", { "sketchPlane" : qUnion([Q0])});
            skPoint(sketch, "E101.centerSnap0", {"position": v(407, 450) * mm});
            skPoint(sketch, "E101.centerSnap1", {"position": v(588, 561) * mm});
            skLineSegment(sketch, "E102.bottom", {"start": v(555.5, 547.73) * mm, "end": v(620.5, 547.73) * mm});
            skPoint(sketch, "E102.left.end.orphan", {"position": v(555.5, 574.27) * mm});
            skPoint(sketch, "E102.right.end.orphan", {"position": v(620.5, 574.27) * mm});
            skLineSegment(sketch, "E103", {"start": v(555.5, 547.73) * mm, "end": v(555.5, 561) * mm});
            skLineSegment(sketch, "E104", {"start": v(555.5, 561) * mm, "end": v(620.5, 561) * mm});
            skLineSegment(sketch, "E105", {"start": v(620.5, 561) * mm, "end": v(620.5, 547.73) * mm});
            skSolve(sketch);
        }
        {
            var Q0;
            Q0 = qSketchRegion(id + "F15", true);
            extrude(context, id + "F16", {"entities" : qUnion([Q0]), "operationType" : NewBodyOperationType.REMOVE, "oppositeDirection" : true, "depth" : 25 * mm, "offsetDistance" : 25 * mm});
        }
        {
            var Q0;
            Q0 = qSketchRegion(id + "F13", true);
            extrude(context, id + "F17", {"entities" : qUnion([Q0]), "operationType" : NewBodyOperationType.REMOVE, "oppositeDirection" : true, "depth" : 25 * mm, "offsetDistance" : 25 * mm});
        }
        {
            var Q0;
            Q0=makeQuery(id+"F12.opExtrude","CAP_FACE",FACE,{"disambiguationData":[OSD([sQuery(id+"F11.wireOp",EDGE,"E93.0"),sQuery(id+"F11.wireOp",EDGE,"E93.1"),sQuery(id+"F11.wireOp",EDGE,"E93.2"),sQuery(id+"F11.wireOp",EDGE,"E93.3")])],"isStart":true});
            var sketch = newSketch(context, id + "F18", { "sketchPlane" : qUnion([Q0])});
            skLineSegment(sketch, "E106.bottom", {"start": v(121.5, 1101.77) * mm, "end": v(186.5, 1101.77) * mm});
            skLineSegment(sketch, "E106.left", {"start": v(121.5, 1101.77) * mm, "end": v(121.5, 1117) * mm});
            skLineSegment(sketch, "E106.right", {"start": v(186.5, 1101.77) * mm, "end": v(186.5, 1117) * mm});
            skPoint(sketch, "E106.middle", {"position": v(154, 1117) * mm});
            skLineSegment(sketch, "E107", {"start": v(121.5, 1117) * mm, "end": v(186.5, 1117) * mm});
            skPoint(sketch, "E108.orphan", {"position": v(186.5, 1132.23) * mm});
            skPoint(sketch, "E109.orphan", {"position": v(121.5, 1132.23) * mm});
            skSolve(sketch);
        }
        {
            var Q0;
            Q0 = qSketchRegion(id + "F18", true);
            extrude(context, id + "F19", {"entities" : qUnion([Q0]), "operationType" : NewBodyOperationType.REMOVE, "oppositeDirection" : true, "depth" : 25 * mm, "offsetDistance" : 25 * mm});
        }
        {
            var Q0;
            Q0=makeQuery(id+"F12.opExtrude","CAP_FACE",FACE,{"disambiguationData":[OSD([sQuery(id+"F11.wireOp",EDGE,"E92.0"),sQuery(id+"F11.wireOp",EDGE,"E92.1"),sQuery(id+"F11.wireOp",EDGE,"E92.2"),sQuery(id+"F11.wireOp",EDGE,"E92.3")])],"isStart":true});
            var sketch = newSketch(context, id + "F20", { "sketchPlane" : qUnion([Q0])});
            skLineSegment(sketch, "E110.bottom", {"start": v(121.5, 1443.64) * mm, "end": v(186.5, 1443.64) * mm});
            skLineSegment(sketch, "E110.left", {"start": v(121.5, 1443.64) * mm, "end": v(121.5, 1455) * mm});
            skLineSegment(sketch, "E110.right", {"start": v(186.5, 1443.64) * mm, "end": v(186.5, 1455) * mm});
            skPoint(sketch, "E110.middle", {"position": v(154, 1455) * mm});
            skLineSegment(sketch, "E111", {"start": v(121.5, 1455) * mm, "end": v(186.5, 1455) * mm});
            skPoint(sketch, "E110.top.start.orphan", {"position": v(121.5, 1466.36) * mm});
            skPoint(sketch, "E112.orphan", {"position": v(186.5, 1466.36) * mm});
            skSolve(sketch);
        }
        {
            var Q0;
            Q0 = qSketchRegion(id + "F20", true);
            extrude(context, id + "F21", {"entities" : qUnion([Q0]), "operationType" : NewBodyOperationType.REMOVE, "oppositeDirection" : true, "depth" : 25 * mm, "offsetDistance" : 25 * mm});
        }
        {
            var Q0;
            Q0=makeQuery(id+"F12.opExtrude","CAP_FACE",FACE,{"disambiguationData":[OSD([sQuery(id+"F11.wireOp",EDGE,"E91.0"),sQuery(id+"F11.wireOp",EDGE,"E91.1"),sQuery(id+"F11.wireOp",EDGE,"E91.2"),sQuery(id+"F11.wireOp",EDGE,"E91.3")])],"isStart":true});
            var sketch = newSketch(context, id + "F22", { "sketchPlane" : qUnion([Q0])});
            skLineSegment(sketch, "E113.bottom", {"start": v(121.5, 1487.4) * mm, "end": v(186.5, 1487.4) * mm});
            skLineSegment(sketch, "E113.left", {"start": v(121.5, 1487.4) * mm, "end": v(121.5, 1479) * mm});
            skLineSegment(sketch, "E113.right", {"start": v(186.5, 1487.4) * mm, "end": v(186.5, 1479) * mm});
            skPoint(sketch, "E113.middle", {"position": v(154, 1479) * mm});
            skLineSegment(sketch, "E114", {"start": v(121.5, 1479) * mm, "end": v(186.5, 1479) * mm});
            skPoint(sketch, "E113.top.start.orphan", {"position": v(121.5, 1470.6) * mm});
            skPoint(sketch, "E115.orphan", {"position": v(186.5, 1470.6) * mm});
            skSolve(sketch);
        }
        {
            var Q0;
            Q0 = qSketchRegion(id + "F22", true);
            extrude(context, id + "F23", {"entities" : qUnion([Q0]), "operationType" : NewBodyOperationType.REMOVE, "oppositeDirection" : true, "depth" : 25 * mm, "offsetDistance" : 25 * mm});
        }
        {
            var Q0;
            Q0=makeQuery(id+"F1.opExtrude","SWEPT_FACE",FACE,{"disambiguationData":[OSD([sQuery(id+"F0.wireOp",EDGE,"E15.trimOffspring")])]});
            var sketch = newSketch(context, id + "F24", { "sketchPlane" : qUnion([Q0])});
            skLineSegment(sketch, "E116", {"start": v(0, 1952) * mm, "end": v(225, 1952) * mm, "construction": true});
            skLineSegment(sketch, "E117", {"start": v(225, 1952) * mm, "end": v(225, 2002) * mm, "construction": true});
            skCircle(sketch, "E118", {"center": v(225, 1952) * mm, "radius": 12.5 * mm});
            skSolve(sketch);
        }
        {
            var Q0;
            Q0 = qSketchRegion(id + "F24", true);
            extrude(context, id + "F25", {"entities" : qUnion([Q0]), "endBound" : BoundingType.UP_TO_NEXT, "depth" : 25 * mm, "offsetDistance" : 25 * mm});
        }
        {
            var Q0;
            Q0=makeQuery(id+"F1.opExtrude","SWEPT_FACE",FACE,{"disambiguationData":[OSD([sQuery(id+"F0.wireOp",EDGE,"E10.trimOffspring")])]});
            var sketch = newSketch(context, id + "F26", { "sketchPlane" : qUnion([Q0])});
            skLineSegment(sketch, "E119.bottom", {"start": v(0, 1744) * mm, "end": v(-300, 1744) * mm});
            skLineSegment(sketch, "E119.top", {"start": v(0, 1726) * mm, "end": v(-300, 1726) * mm});
            skLineSegment(sketch, "E119.left", {"start": v(0, 1744) * mm, "end": v(0, 1726) * mm});
            skLineSegment(sketch, "E119.right", {"start": v(-300, 1744) * mm, "end": v(-300, 1726) * mm});
            skSolve(sketch);
        }
        {
            var Q0;
            Q0 = qSketchRegion(id + "F26", true);
            extrude(context, id + "F27", {"entities" : qUnion([Q0]), "endBound" : BoundingType.UP_TO_NEXT, "depth" : 25 * mm, "offsetDistance" : 25 * mm});
        }
        {
            var Q0;
            Q0=makeQuery(id+"F3.opExtrude","CAP_FACE",FACE,{"disambiguationData":[OSD([sQuery(id+"F2.wireOp",EDGE,"E23.bottom"),sQuery(id+"F2.wireOp",EDGE,"E23.top"),sQuery(id+"F2.wireOp",EDGE,"E23.left"),sQuery(id+"F2.wireOp",EDGE,"E23.right")])],"isStart":false});
            var sketch = newSketch(context, id + "F28", { "sketchPlane" : qUnion([Q0])});
            skLineSegment(sketch, "E120", {"start": v(0, 2020) * mm, "end": v(-10, 2020) * mm, "construction": true});
            skLineSegment(sketch, "E121", {"start": v(-10, 2020) * mm, "end": v(-10, 2030) * mm, "construction": true});
            skLineSegment(sketch, "E122.bottom", {"start": v(-10, 2030) * mm, "end": v(-520, 2030) * mm});
            skLineSegment(sketch, "E122.top", {"start": v(-10, 2340) * mm, "end": v(-520, 2340) * mm});
            skLineSegment(sketch, "E122.left", {"start": v(-10, 2030) * mm, "end": v(-10, 2340) * mm});
            skLineSegment(sketch, "E122.right", {"start": v(-520, 2030) * mm, "end": v(-520, 2340) * mm});
            skSolve(sketch);
        }
        {
            var Q0;
            Q0 = qSketchRegion(id + "F28", true);
            extrude(context, id + "F29", {"entities" : qUnion([Q0]), "oppositeDirection" : true, "depth" : 370 * mm, "offsetDistance" : 25 * mm});
        }
        {
            var Q0;
            Q0=makeQuery(id+"F29.opExtrude","CAP_FACE",FACE,{"disambiguationData":[OSD([sQuery(id+"F28.wireOp",EDGE,"E122.bottom"),sQuery(id+"F28.wireOp",EDGE,"E122.top"),sQuery(id+"F28.wireOp",EDGE,"E122.left"),sQuery(id+"F28.wireOp",EDGE,"E122.right")])],"isStart":false});
            var sketch = newSketch(context, id + "F30", { "sketchPlane" : qUnion([Q0])});
            skLineSegment(sketch, "E123.bottom", {"start": v(40, 2060) * mm, "end": v(420, 2060) * mm});
            skLineSegment(sketch, "E123.top", {"start": v(40, 2310) * mm, "end": v(420, 2310) * mm});
            skLineSegment(sketch, "E123.left", {"start": v(40, 2060) * mm, "end": v(40, 2310) * mm});
            skLineSegment(sketch, "E123.right", {"start": v(420, 2060) * mm, "end": v(420, 2310) * mm});
            skSolve(sketch);
        }
        {
            var Q0;
            Q0 = qSketchRegion(id + "F30", true);
            extrude(context, id + "F31", {"entities" : qUnion([Q0]), "operationType" : NewBodyOperationType.REMOVE, "oppositeDirection" : true, "depth" : 5 * mm, "offsetDistance" : 25 * mm});
        }
    });
